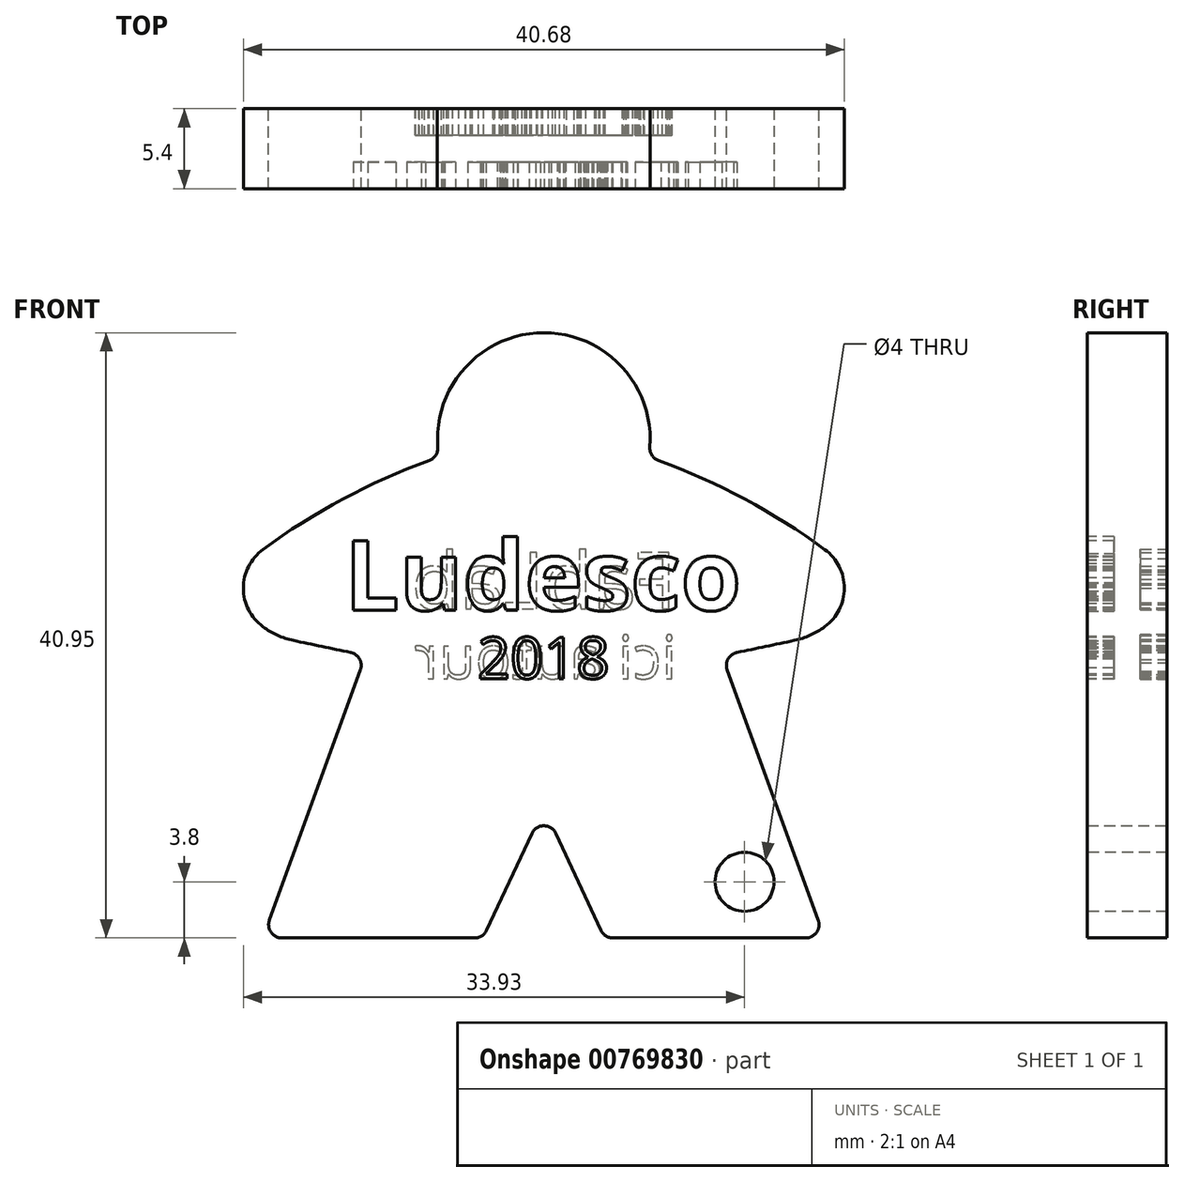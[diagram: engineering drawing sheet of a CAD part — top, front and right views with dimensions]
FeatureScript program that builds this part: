
annotation { "Feature Type Name" : "Feature", "Feature Type Description" : "" }
export const myFeature = defineFeature(function(context is Context, id is Id, definition is map)
    precondition{}
    {
        {
            var Q0;
            Q0=qCreatedBy(makeId("Front.planeOp"),FACE);
            var sketch = newSketch(context, id + "F0", { "sketchPlane" : qUnion([Q0])});
            skArc(sketch, "E0", {"start": v(0, 28) * mm, "mid": v(-5.87, 25.44) * mm, "end": v(-7.98, 19.4) * mm});
            skArc(sketch, "E1", {"start": v(-8.63, 18.38) * mm, "mid": v(-15.12, 15.49) * mm, "end": v(-21.13, 11.7) * mm});
            skArc(sketch, "E2", {"start": v(-21.13, 11.7) * mm, "mid": v(-22.6, 8.8) * mm, "end": v(-21.13, 5.9) * mm});
            skPoint(sketch, "E3.startSnap0", {"position": v(0, 28) * mm});
            skPoint(sketch, "E3.start.orphan", {"position": v(0, 28) * mm});
            skLineSegment(sketch, "E4", {"start": v(0, 28) * mm, "end": v(-6.73, 28) * mm, "construction": true});
            skArc(sketch, "E5", {"start": v(-21.13, 5.9) * mm, "mid": v(-20.04, 5.26) * mm, "end": v(-18.84, 4.87) * mm});
            skArc(sketch, "E6", {"start": v(-18.84, 4.87) * mm, "mid": v(-16.7, 4.41) * mm, "end": v(-14.54, 3.97) * mm});
            skLineSegment(sketch, "E7", {"start": v(-19.7, -17.5) * mm, "end": v(-5.2, -17.5) * mm});
            skLineSegment(sketch, "E8", {"start": v(-4.3, -16.92) * mm, "end": v(-0.9, -9.64) * mm});
            skLineSegment(sketch, "E9", {"start": v(-13.8, 2.65) * mm, "end": v(-20.64, -16.16) * mm});
            skPoint(sketch, "E10.visualSharp", {"position": v(-21.13, -17.5) * mm});
            skArc(sketch, "E10.filletArc", {"start": v(-20.64, -16.16) * mm, "mid": v(-20.52, -17.07) * mm, "end": v(-19.7, -17.5) * mm});
            skPoint(sketch, "E11.visualSharp", {"position": v(-4.57, -17.5) * mm});
            skArc(sketch, "E11.filletArc", {"start": v(-5.2, -17.5) * mm, "mid": v(-4.67, -17.34) * mm, "end": v(-4.3, -16.92) * mm});
            skPoint(sketch, "E12.visualSharp", {"position": v(-7.89, 18.65) * mm});
            skArc(sketch, "E12.filletArc", {"start": v(-8.63, 18.38) * mm, "mid": v(-8.13, 18.78) * mm, "end": v(-7.98, 19.4) * mm});
            skPoint(sketch, "E13.visualSharp", {"position": v(-13.4, 3.74) * mm});
            skArc(sketch, "E13.filletArc", {"start": v(-13.8, 2.65) * mm, "mid": v(-13.86, 3.48) * mm, "end": v(-14.54, 3.97) * mm});
            skArc(sketch, "E14.MirrorCS", {"start": v(0, 28) * mm, "mid": v(5.87, 25.44) * mm, "end": v(7.98, 19.4) * mm});
            skArc(sketch, "E15.MirrorCS", {"start": v(8.63, 18.38) * mm, "mid": v(15.12, 15.49) * mm, "end": v(21.13, 11.7) * mm});
            skArc(sketch, "E16.MirrorCS", {"start": v(8.63, 18.38) * mm, "mid": v(8.13, 18.78) * mm, "end": v(7.98, 19.4) * mm});
            skArc(sketch, "E17.MirrorCS", {"start": v(21.13, 11.7) * mm, "mid": v(22.6, 8.8) * mm, "end": v(21.13, 5.9) * mm});
            skArc(sketch, "E18.MirrorCS", {"start": v(21.13, 5.9) * mm, "mid": v(20.04, 5.26) * mm, "end": v(18.84, 4.87) * mm});
            skArc(sketch, "E19.MirrorCS", {"start": v(18.84, 4.87) * mm, "mid": v(16.7, 4.41) * mm, "end": v(14.54, 3.97) * mm});
            skArc(sketch, "E20.MirrorCS", {"start": v(13.8, 2.65) * mm, "mid": v(13.86, 3.48) * mm, "end": v(14.54, 3.97) * mm});
            skLineSegment(sketch, "E21.MirrorCS", {"start": v(13.8, 2.65) * mm, "end": v(20.64, -16.16) * mm});
            skArc(sketch, "E22.MirrorCS", {"start": v(20.64, -16.16) * mm, "mid": v(20.52, -17.07) * mm, "end": v(19.7, -17.5) * mm});
            skLineSegment(sketch, "E23.MirrorCS", {"start": v(19.7, -17.5) * mm, "end": v(5.2, -17.5) * mm});
            skArc(sketch, "E24.MirrorCS", {"start": v(5.2, -17.5) * mm, "mid": v(4.67, -17.34) * mm, "end": v(4.3, -16.92) * mm});
            skLineSegment(sketch, "E25.MirrorCS", {"start": v(4.3, -16.92) * mm, "end": v(0.9, -9.64) * mm});
            skPoint(sketch, "E26.visualSharp", {"position": v(0, -7.7) * mm});
            skArc(sketch, "E26.filletArc", {"start": v(0.9, -9.64) * mm, "mid": v(0, -9.07) * mm, "end": v(-0.9, -9.64) * mm});
            skSolve(sketch);
        }
        {
            var Q0;
            Q0=makeQuery(id+"F0.imprint","IMPRINT",FACE,{"disambiguationData":[TD([[makeQuery(id+"F0.imprint","IMPRINT",EDGE,{"derivedFrom":sQuery(id+"F0.wireOp",EDGE,"E0")}),1.0]])]});
            extrude(context, id + "F1", {"entities" : qUnion([Q0]), "endBound" : BoundingType.SYMMETRIC, "depth" : 6 * mm, "offsetDistance" : 25 * mm});
        }
        {
            var Q0;
            Q0=qCreatedBy(makeId("Front.planeOp"),FACE);
            var sketch = newSketch(context, id + "F2", { "sketchPlane" : qUnion([Q0])});
            skCircle(sketch, "E27", {"center": v(0, 28) * mm, "radius": 4 * mm});
            skCircle(sketch, "E28.0", {"center": v(0, 28) * mm, "radius": 2 * mm});
            skSolve(sketch);
        }
        {
            var Q0;
            Q0=makeQuery(id+"F1.opExtrude","CAP_FACE",FACE,{"disambiguationData":[OSD([sQuery(id+"F0.wireOp",EDGE,"E0"),sQuery(id+"F0.wireOp",EDGE,"E1"),sQuery(id+"F0.wireOp",EDGE,"E2"),sQuery(id+"F0.wireOp",EDGE,"E5"),sQuery(id+"F0.wireOp",EDGE,"E6"),sQuery(id+"F0.wireOp",EDGE,"E7"),sQuery(id+"F0.wireOp",EDGE,"E8"),sQuery(id+"F0.wireOp",EDGE,"E9"),sQuery(id+"F0.wireOp",EDGE,"E10.filletArc"),sQuery(id+"F0.wireOp",EDGE,"E11.filletArc"),sQuery(id+"F0.wireOp",EDGE,"E12.filletArc"),sQuery(id+"F0.wireOp",EDGE,"E13.filletArc"),sQuery(id+"F0.wireOp",EDGE,"E14.MirrorCS"),sQuery(id+"F0.wireOp",EDGE,"E15.MirrorCS"),sQuery(id+"F0.wireOp",EDGE,"E16.MirrorCS"),sQuery(id+"F0.wireOp",EDGE,"E17.MirrorCS"),sQuery(id+"F0.wireOp",EDGE,"E18.MirrorCS"),sQuery(id+"F0.wireOp",EDGE,"E19.MirrorCS"),sQuery(id+"F0.wireOp",EDGE,"E20.MirrorCS"),sQuery(id+"F0.wireOp",EDGE,"E21.MirrorCS"),sQuery(id+"F0.wireOp",EDGE,"E22.MirrorCS"),sQuery(id+"F0.wireOp",EDGE,"E23.MirrorCS"),sQuery(id+"F0.wireOp",EDGE,"E24.MirrorCS"),sQuery(id+"F0.wireOp",EDGE,"E25.MirrorCS"),sQuery(id+"F0.wireOp",EDGE,"E26.filletArc")])],"isStart":false});
            var sketch = newSketch(context, id + "F3", { "sketchPlane" : qUnion([Q0])});
            skText(sketch, "E29", { "text": "Ludesco", "fontName": "OpenSans-Bold.ttf"});
            skText(sketch, "E30", { "text": "2018", "fontName": "OpenSans-Regular.ttf"});
            const initialGuessF3  = {"E29": [-0.015, 0.00713, 1, 0, 0.00527], "E30": [-0.005, 0.002, 1, 0, 0.00313]};
            skSetInitialGuess(sketch, initialGuessF3);
            skSolve(sketch);
        }
        {
            var Q0;
            Q0 = qSketchRegion(id + "F3", true);
            extrude(context, id + "F4", {"entities" : qUnion([Q0]), "operationType" : NewBodyOperationType.REMOVE, "oppositeDirection" : true, "depth" : 2 * mm, "offsetDistance" : 25 * mm});
        }
        {
            var Q0;
            Q0=makeQuery(id+"F1.opExtrude","CAP_FACE",FACE,{"disambiguationData":[OSD([sQuery(id+"F0.wireOp",EDGE,"E0"),sQuery(id+"F0.wireOp",EDGE,"E1"),sQuery(id+"F0.wireOp",EDGE,"E2"),sQuery(id+"F0.wireOp",EDGE,"E5"),sQuery(id+"F0.wireOp",EDGE,"E6"),sQuery(id+"F0.wireOp",EDGE,"E7"),sQuery(id+"F0.wireOp",EDGE,"E8"),sQuery(id+"F0.wireOp",EDGE,"E9"),sQuery(id+"F0.wireOp",EDGE,"E10.filletArc"),sQuery(id+"F0.wireOp",EDGE,"E11.filletArc"),sQuery(id+"F0.wireOp",EDGE,"E12.filletArc"),sQuery(id+"F0.wireOp",EDGE,"E13.filletArc"),sQuery(id+"F0.wireOp",EDGE,"E14.MirrorCS"),sQuery(id+"F0.wireOp",EDGE,"E15.MirrorCS"),sQuery(id+"F0.wireOp",EDGE,"E16.MirrorCS"),sQuery(id+"F0.wireOp",EDGE,"E17.MirrorCS"),sQuery(id+"F0.wireOp",EDGE,"E18.MirrorCS"),sQuery(id+"F0.wireOp",EDGE,"E19.MirrorCS"),sQuery(id+"F0.wireOp",EDGE,"E20.MirrorCS"),sQuery(id+"F0.wireOp",EDGE,"E21.MirrorCS"),sQuery(id+"F0.wireOp",EDGE,"E22.MirrorCS"),sQuery(id+"F0.wireOp",EDGE,"E23.MirrorCS"),sQuery(id+"F0.wireOp",EDGE,"E24.MirrorCS"),sQuery(id+"F0.wireOp",EDGE,"E25.MirrorCS"),sQuery(id+"F0.wireOp",EDGE,"E26.filletArc")])],"isStart":true});
            var sketch = newSketch(context, id + "F5", { "sketchPlane" : qUnion([Q0])});
            skText(sketch, "E31", { "text": "FabLab\n", "fontName": "OpenSans-Regular.ttf"});
            skText(sketch, "E32", { "text": "ici autour\n", "fontName": "OpenSans-Regular.ttf"});
            const initialGuessF5  = {"E31": [-0.01, 0.00724, 1, 0, 0.00426], "E32": [-0.01, 0.002, 1, 0, 0.00324]};
            skSetInitialGuess(sketch, initialGuessF5);
            skSolve(sketch);
        }
        {
            var Q0;
            Q0 = qSketchRegion(id + "F5", true);
            extrude(context, id + "F6", {"entities" : qUnion([Q0]), "operationType" : NewBodyOperationType.REMOVE, "oppositeDirection" : true, "depth" : 2 * mm, "offsetDistance" : 25 * mm});
        }
        {
            var Q0;
            Q0=makeQuery(id+"F1.opExtrude","SWEPT_BODY",BODY,{"disambiguationData":[OSD([sQuery(id+"F0.wireOp",EDGE,"E0"),sQuery(id+"F0.wireOp",EDGE,"E1"),sQuery(id+"F0.wireOp",EDGE,"E2"),sQuery(id+"F0.wireOp",EDGE,"E5"),sQuery(id+"F0.wireOp",EDGE,"E6"),sQuery(id+"F0.wireOp",EDGE,"E7"),sQuery(id+"F0.wireOp",EDGE,"E8"),sQuery(id+"F0.wireOp",EDGE,"E9"),sQuery(id+"F0.wireOp",EDGE,"E10.filletArc"),sQuery(id+"F0.wireOp",EDGE,"E11.filletArc"),sQuery(id+"F0.wireOp",EDGE,"E12.filletArc"),sQuery(id+"F0.wireOp",EDGE,"E13.filletArc"),sQuery(id+"F0.wireOp",EDGE,"E14.MirrorCS"),sQuery(id+"F0.wireOp",EDGE,"E15.MirrorCS"),sQuery(id+"F0.wireOp",EDGE,"E16.MirrorCS"),sQuery(id+"F0.wireOp",EDGE,"E17.MirrorCS"),sQuery(id+"F0.wireOp",EDGE,"E18.MirrorCS"),sQuery(id+"F0.wireOp",EDGE,"E19.MirrorCS"),sQuery(id+"F0.wireOp",EDGE,"E20.MirrorCS"),sQuery(id+"F0.wireOp",EDGE,"E21.MirrorCS"),sQuery(id+"F0.wireOp",EDGE,"E22.MirrorCS"),sQuery(id+"F0.wireOp",EDGE,"E23.MirrorCS"),sQuery(id+"F0.wireOp",EDGE,"E24.MirrorCS"),sQuery(id+"F0.wireOp",EDGE,"E25.MirrorCS"),sQuery(id+"F0.wireOp",EDGE,"E26.filletArc")])]});
            var Q1;
            Q1=qCreatedBy(makeId("Origin.pointOp"),VERTEX);
            transform(context, id + "F7", {"entities" : qUnion([Q0]), "transformType" : TransformType.SCALE_UNIFORMLY, "scale" : 0.9, "scalePoint" : qUnion([Q1]), "makeCopy" : false});
        }
        {
            var Q0;
            {var subQ0=sQuery(id+"F0.wireOp",EDGE,"E24.MirrorCS");var subQ1=sQuery(id+"F0.wireOp",EDGE,"E23.MirrorCS");var subQ2=sQuery(id+"F0.wireOp",EDGE,"E22.MirrorCS");var subQ3=sQuery(id+"F0.wireOp",EDGE,"E21.MirrorCS");var subQ4=sQuery(id+"F0.wireOp",EDGE,"E20.MirrorCS");var subQ5=sQuery(id+"F0.wireOp",EDGE,"E19.MirrorCS");var subQ6=sQuery(id+"F0.wireOp",EDGE,"E18.MirrorCS");var subQ7=sQuery(id+"F0.wireOp",EDGE,"E17.MirrorCS");var subQ8=sQuery(id+"F0.wireOp",EDGE,"E16.MirrorCS");var subQ9=sQuery(id+"F0.wireOp",EDGE,"E15.MirrorCS");var subQ10=sQuery(id+"F0.wireOp",EDGE,"E13.filletArc");var subQ11=sQuery(id+"F0.wireOp",EDGE,"E12.filletArc");var subQ12=sQuery(id+"F0.wireOp",EDGE,"E5");var subQ13=sQuery(id+"F0.wireOp",EDGE,"E2");var subQ14=sQuery(id+"F0.wireOp",EDGE,"E1");var subQ15=sQuery(id+"F0.wireOp",EDGE,"E14.MirrorCS");var subQ16=sQuery(id+"F0.wireOp",EDGE,"E0");var subQ17=sQuery(id+"F0.wireOp",EDGE,"E6");var subQ18=sQuery(id+"F0.wireOp",EDGE,"E7");var subQ19=sQuery(id+"F0.wireOp",EDGE,"E8");var subQ20=sQuery(id+"F0.wireOp",EDGE,"E9");var subQ21=sQuery(id+"F0.wireOp",EDGE,"E10.filletArc");var subQ22=sQuery(id+"F0.wireOp",EDGE,"E11.filletArc");var subQ23=sQuery(id+"F0.wireOp",EDGE,"E25.MirrorCS");var subQ24=sQuery(id+"F0.wireOp",EDGE,"E26.filletArc");Q0=makeQuery(id+"F4.boolean.opBoolean","SPLIT",FACE,{"disambiguationData":[TD([makeQuery(id+"F1.opExtrude","SWEPT_FACE",FACE,{"disambiguationData":[OSD([subQ14])]})])],"derivedFrom":makeQuery(id+"F1.opExtrude","CAP_FACE",FACE,{"disambiguationData":[OSD([subQ16,subQ14,subQ13,subQ12,subQ17,subQ18,subQ19,subQ20,subQ21,subQ22,subQ11,subQ10,subQ15,subQ9,subQ8,subQ7,subQ6,subQ5,subQ4,subQ3,subQ2,subQ1,subQ0,subQ23,subQ24])],"isStart":false})});}
            var sketch = newSketch(context, id + "F8", { "sketchPlane" : qUnion([Q0])});
            skCircle(sketch, "E33", {"center": v(13.6, -11.95) * mm, "radius": 2 * mm});
            skSolve(sketch);
        }
        {
            var Q0;
            Q0=makeQuery(id+"F8.imprint","IMPRINT",FACE,{"disambiguationData":[TD([[makeQuery(id+"F8.imprint","IMPRINT",EDGE,{"derivedFrom":sQuery(id+"F8.wireOp",EDGE,"E33")}),1.0]])]});
            extrude(context, id + "F9", {"entities" : qUnion([Q0]), "operationType" : NewBodyOperationType.REMOVE, "oppositeDirection" : true, "depth" : 25 * mm, "offsetDistance" : 25 * mm});
        }
    });
